# Revit family: EFLLED_Wall Hosted-R16
name_source: partatom
category: Lighting Fixtures
revit_build: Autodesk Revit LT 2016 (Build: 20150220_1215(x64)
units: mm (PartAtom-declared; Revit-internal decimal feet)

## family parameters
Always vertical = Yes
Cut with Voids When Loaded = No
Host = Wall
Light Source = Yes
OmniClass Number = 23.80.70.00
OmniClass Title = Lighting
Part Type = Normal
Room Calculation Point = No
Round Connector Dimension = Use Diameter
Shared = No

## types (1)
- Type 1
    Ballast = Electronic
    Charging = NiCd Pulse Charge
    Color Filter = 16777215
    Construction = Economy LED Supalite Flood Unit, surface mount emergency light
    Dimming Lamp Color Temperature Shift = <None>
    Height = 1807 mm
    IP Rating = IP20
    Lamp = 2 x LED
    Mounting = Surface Wall Mount & supplied with flex and plug (the flex and plug can be removed to allow for a hard wired connection)
    Operating Mode = Non-Maintained
    Operating Temperature = 1°C to 40°C (Ambient)
    Operating Voltage = 240V AC
    Photometric Web File = ll18731 - EFLLED (CT10130-A6 NiCd LifeLightPro P1.04-2C543 NVSW119BT-V1-E).IES
    Power Consumption = 2.0W standby (3.3W Max during the first 16 hours charge)
    Testing System = Manual Switch Test
    Tilt Angle = 0.00°

## geometry (parser evidence)
native form markers: Sweep x3
no freeform markers — native parametric forms only
